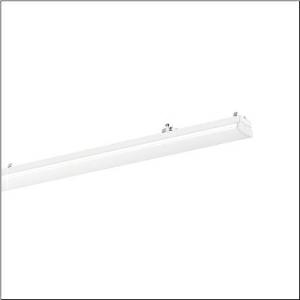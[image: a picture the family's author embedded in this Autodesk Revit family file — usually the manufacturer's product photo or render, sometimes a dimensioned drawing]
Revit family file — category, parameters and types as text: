
# Revit family: licross_11_recessed_opal_mo_51tl1d7n46xg
name_source: partatom
category: Lighting Fixtures
units: mm (PartAtom-declared; Revit-internal decimal feet)

## family parameters
Cut with Voids When Loaded = No
Host = Face
Light Source = No
Part Type = Normal
Room Calculation Point = No
Round Connector Dimension = Use Diameter
Shared = No

## types (1)
- Licross 11 recessed opal MO (1 x LED, 6300 lm, 35.1 W, 4000K)
    Apparent Load = 35 VA
    CIE Flux Codes = 44 73 91 87 100
    Color Rendering = 80
    Color Temperature = 4000K
    Default Elevation = 1800 mm
    Description = Licross 11 recessed opal MO, luminaire insert, of sheet steel, coil coated, white, length: 1.500mm, width: 76mm, height: 87mm, LED rated luminous flux: 6.300lm, light colour: 840, SDCM (Standard Deviation of Colour Matching)MacAdam ≤ 2 SDCM (initial), control gear: ON/OFF, with plug, 3-pole, with phase selection, mains connection: 220..240V, AC, 50/60Hz, rated input power: 35W, internal wiring halogen-free, primary optical cover: cover, of PMMA, light emission: direct with ceiling illumination distribution, primary light characteristic: symmetric, protection rating (complete): IP40, insulation class (complete): insulation class I (protective earthing), certification: CE, ENEC, VDE, UKCA, protection symbol: D if used in an environment without relevant dust loads with corresponding accessories, impact resistance: IK06, permissible ambient temperature for indoor applications: -35..+45°C, corresponds to IFS (International Featured Standards) requirements for safety and quality in the food industry, reducing of maximum allowable ambient temperature of 5°C with ceiling mounting, The light source and the operating device comply with the requirements of the Ecodesign Regulation (EU) 2019/2020 and are replaceable in accordance with this regulation, packaging unit: 1 piece
    Height = 83 mm
    Lamp = 1 x LED
    Lamp Light Flux = 6300 lm
    Lamp Power = 35.1 W
    Lamp count = 1
    Length = 1500 mm
    Luminous efficacy = 179 lm/W
    Manufacturer = Siteco
    ModVariant = No
    Model = 51TL1D7N46XG
    Mounting Place = Ceiling
    Mounting Type = Pendant
    Number of Poles = 1
    OnlyDefault = Yes
    Power Factor = 1
    Product Name = Licross 11 recessed opal MO
    Product group = luminaire insert | ceiling pendant
    ProductGroupID = 901
    Protection Class = Protection class I
    Protection Degree = IP 40
    RLX_Detail_Level = 1
    RLX_Emergency_Light_Flux = 0 lm
    RLX_Emergency_Type = 0
    RLX_Emergency_Type_DB = No
    RlxData = <blob elided: 23345 chars, md5=777452b0>
    Socket = socket
    Standby Power = 0 W
    System Light Flux = 6300 lm
    System Power = 35 W
    Type Comments = Product without accessories
    Type Image = l_1313666.jpg
    URL = http://relux.com
    VarID = ---
    Voltage = 0 V
    Weight = 0.00 kg
    Width = 76 mm

## geometry (parser evidence)
native form markers: Blend x4, Sweep x13
no freeform markers — native parametric forms only
